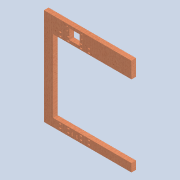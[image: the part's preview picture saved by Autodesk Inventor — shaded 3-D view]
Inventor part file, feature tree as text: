
AUTODESK INVENTOR PART (.ipt)
format: ipt  version: 2020 (Build 240168000, 168)  size: 265,728 bytes
history: native  units: mm
features: extrude x5, sketch x4, other x3, pattern_linear x1, hole x1, reference x1
ambient origin geometry x8: Origin, YZ Plane, XZ Plane, XY Plane, X Axis, Y Axis, Z Axis, Center Point
bodies: Solid1 (feature_tree)
feature tree (15):
  extrude  "Extrusion1"  Depth=420.0mm
  extrude  "Extrusion5"  Depth=70.0mm
  extrude  "Extrusion6"  Depth=40.0mm
  extrude  "Extrusion8"  Depth=10.0mm
  extrude  "Extrusion9"  Depth=10.0mm
  pattern_linear  "Rectangular Pattern1"  Spacing1=4.5mm  [1 undecoded]
  hole  "Hole1"  [1 undecoded]
  sketch  "Sketch1"  dims[d0=380.0mm d1=420.0mm]
  sketch  "Sketch6"  dims[d2=20.0mm d3=0.0mm d24=70.0mm]
  sketch  "Sketch9"  dims[d25=35.0mm d26=40.0mm]
  reference  "Reference13"
  sketch  "Sketch10"  dims[d27=0.0mm d28=0.0mm d30=15.0mm d32=123.194mm d33=4.5mm d34=10.0mm d36=20.0mm d37=0.0mm d38=0.0mm d43=0.0mm d44=0.0mm d45=44.0mm d50=35.0mm d51=16.0mm d52=5.0mm d53=4.5mm d54=68.694mm d55=47.0mm d56=70.7mm d59=0.0mm d60=0.0mm d61=20.0mm d63=90.0mm d64=20.0mm d66=345.0mm d67=132.694mm d68=7.0mm d69=64.0mm d70=10.0mm d71=17.0mm d72=5.0mm d73=6.0mm d74=4.0mm d75=2.0mm d76=90.0deg d77=8.0mm d78=20.594885mm]
  parser-record x1  (decoder bookkeeping rows leaked as tree rows — omitted from the tree; the rows remain in map.json)
  other  "0005-00-00 Ansamblu_General.iam"
  other  "0005-10-015 suport tija.ipt:51"
note: 2 required parameter values undecoded (feature->parameter linkage not recoverable at this tier; creation-order binding heuristic only, values carry confidence <= 0.55)
note: 1 file-system path scrubbed to <path> (originals preserved in map.json)
